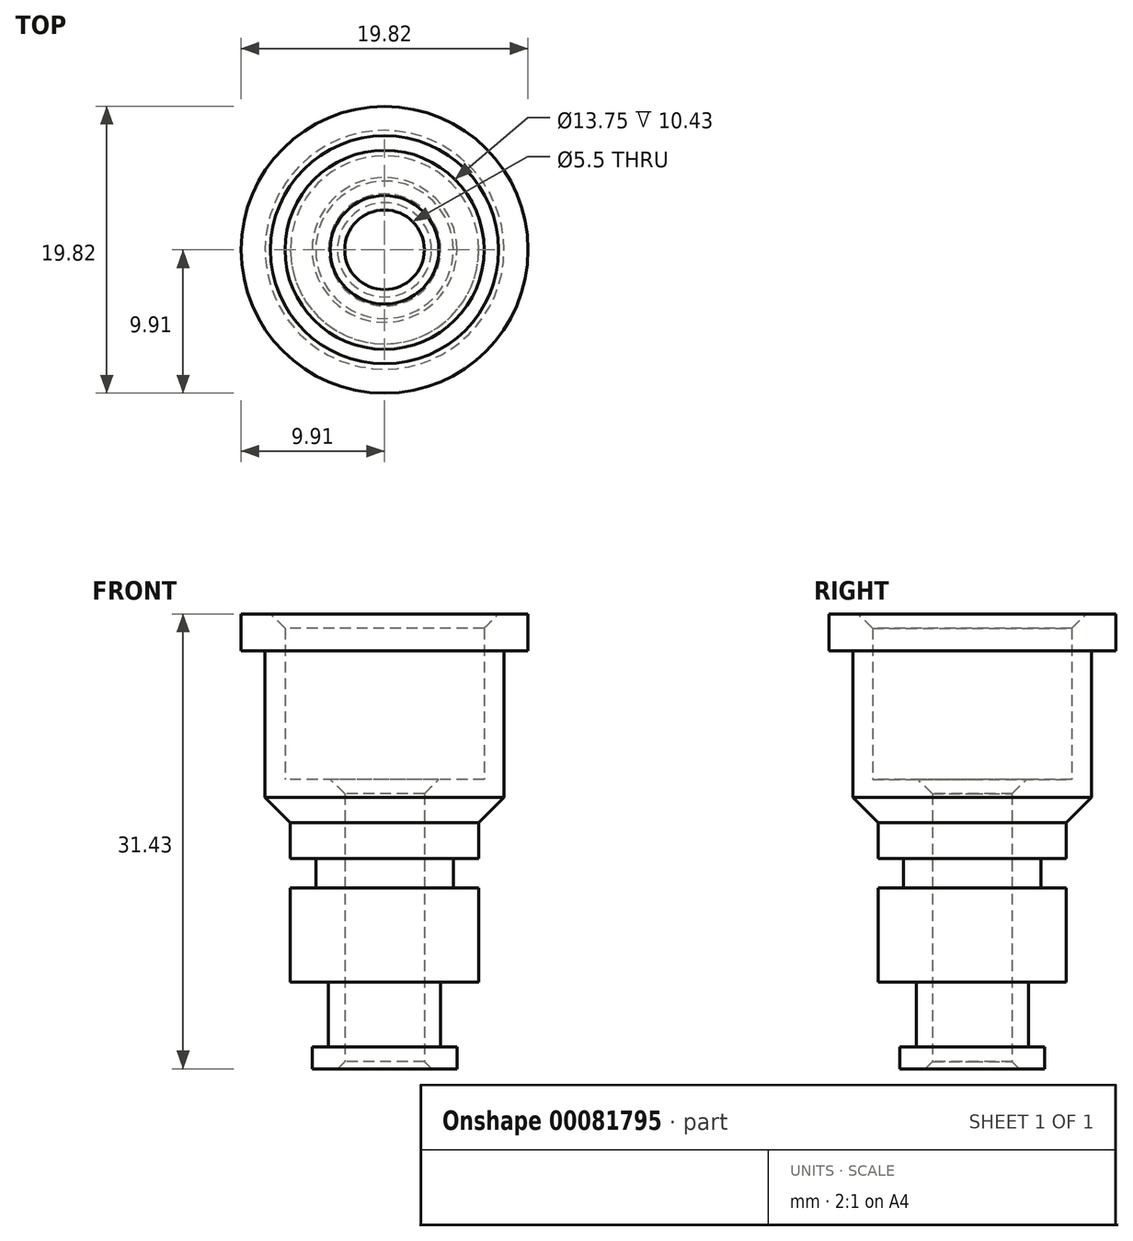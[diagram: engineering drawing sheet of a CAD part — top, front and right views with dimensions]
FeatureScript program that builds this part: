
annotation { "Feature Type Name" : "Feature", "Feature Type Description" : "" }
export const myFeature = defineFeature(function(context is Context, id is Id, definition is map)
    precondition{}
    {
        {
            var Q0;
            Q0=qCreatedBy(makeId("Top.planeOp"),FACE);
            var sketch = newSketch(context, id + "F0", { "sketchPlane" : qUnion([Q0])});
            skCircle(sketch, "E0", {"center": v(0, 0) * mm, "radius": 6.5 * mm});
            skCircle(sketch, "E1", {"center": v(0, 0) * mm, "radius": 2.75 * mm});
            skSolve(sketch);
        }
        {
            var Q0;
            Q0 = qSketchRegion(id + "F0", true);
            extrude(context, id + "F1", {"entities" : qUnion([Q0]), "depth" : 20 * mm});
        }
        {
            var Q0;
            Q0=makeQuery(id+"F1.opExtrude","CAP_FACE",FACE,{"disambiguationData":[OSD([sQuery(id+"F0.wireOp",EDGE,"E0"),sQuery(id+"F0.wireOp",EDGE,"E1")])],"isStart":true});
            var sketch = newSketch(context, id + "F2", { "sketchPlane" : qUnion([Q0])});
            skCircle(sketch, "E2.0", {"center": v(0, 0) * mm, "radius": 6.5 * mm});
            skCircle(sketch, "E3", {"center": v(0, 0) * mm, "radius": 5 * mm});
            skSolve(sketch);
        }
        {
            var Q0;
            Q0 = qSketchRegion(id + "F2", true);
            extrude(context, id + "F3", {"entities" : qUnion([Q0]), "operationType" : NewBodyOperationType.REMOVE, "oppositeDirection" : true, "depth" : 6 * mm});
        }
        {
            var Q0;
            Q0=makeQuery(id+"F3.boolean.opBoolean","COPY",FACE,{"derivedFrom":makeQuery(id+"F3.opExtrude","CAP_FACE",FACE,{"disambiguationData":[OSD([sQuery(id+"F2.wireOp",EDGE,"E2.0"),sQuery(id+"F2.wireOp",EDGE,"E3")])],"isStart":false})});
            var sketch = newSketch(context, id + "F4", { "sketchPlane" : qUnion([Q0])});
            skCircle(sketch, "E4.0", {"center": v(0, 0) * mm, "radius": 5 * mm});
            skCircle(sketch, "E5", {"center": v(0, 0) * mm, "radius": 3.88 * mm});
            skSolve(sketch);
        }
        {
            var Q0;
            Q0 = qSketchRegion(id + "F4", true);
            extrude(context, id + "F5", {"entities" : qUnion([Q0]), "operationType" : NewBodyOperationType.REMOVE, "depth" : 4.5 * mm});
        }
        {
            var Q0;
            Q0=makeQuery(id+"F1.opExtrude","CAP_FACE",FACE,{"disambiguationData":[OSD([sQuery(id+"F0.wireOp",EDGE,"E0"),sQuery(id+"F0.wireOp",EDGE,"E1")])],"isStart":true});
            cPlane(context, id + "F6", {"entities" : qUnion([Q0]), "cplaneType" : CPlaneType.OFFSET, "offset" : 12.5 * mm, "oppositeDirection" : true, "width" : 150 * mm, "height" : 150 * mm});
        }
        {
            var Q0;
            Q0=qCreatedBy(id+"F6.planeOp",FACE);
            var sketch = newSketch(context, id + "F7", { "sketchPlane" : qUnion([Q0])});
            skCircle(sketch, "E6.0", {"center": v(0, 0) * mm, "radius": 6.5 * mm});
            skCircle(sketch, "E7", {"center": v(0, 0) * mm, "radius": 4.75 * mm});
            skSolve(sketch);
        }
        {
            var Q0;
            Q0 = qSketchRegion(id + "F7", true);
            extrude(context, id + "F8", {"entities" : qUnion([Q0]), "operationType" : NewBodyOperationType.REMOVE, "oppositeDirection" : true, "depth" : 2.03 * mm});
        }
        {
            var Q0;
            Q0=makeQuery(id+"F1.opExtrude","CAP_FACE",FACE,{"disambiguationData":[OSD([sQuery(id+"F0.wireOp",EDGE,"E0"),sQuery(id+"F0.wireOp",EDGE,"E1")])],"isStart":false});
            var sketch = newSketch(context, id + "F9", { "sketchPlane" : qUnion([Q0])});
            skCircle(sketch, "E8.0", {"center": v(0, 0) * mm, "radius": 6.5 * mm});
            skCircle(sketch, "E9", {"center": v(0, 0) * mm, "radius": 8.25 * mm});
            skSolve(sketch);
        }
        {
            var Q0;
            Q0 = qSketchRegion(id + "F9", true);
            extrude(context, id + "F10", {"entities" : qUnion([Q0]), "operationType" : NewBodyOperationType.ADD, "oppositeDirection" : true, "depth" : 3 * mm});
        }
        {
            var Q0;
            Q0=makeQuery(id+"F10.boolean.opBoolean","MERGE",FACE,{"derivedFrom":[makeQuery(id+"F1.opExtrude","CAP_FACE",FACE,{"disambiguationData":[OSD([sQuery(id+"F0.wireOp",EDGE,"E0"),sQuery(id+"F0.wireOp",EDGE,"E1")])],"isStart":false}),makeQuery(id+"F10.opExtrude","CAP_FACE",FACE,{"disambiguationData":[OSD([sQuery(id+"F9.wireOp",EDGE,"E8.0"),sQuery(id+"F9.wireOp",EDGE,"E9")])],"isStart":true})]});
            var sketch = newSketch(context, id + "F11", { "sketchPlane" : qUnion([Q0])});
            skCircle(sketch, "E10", {"center": v(0, 0) * mm, "radius": 6.88 * mm});
            skCircle(sketch, "E11.0", {"center": v(0, 0) * mm, "radius": 8.25 * mm});
            skSolve(sketch);
        }
        {
            var Q0;
            Q0 = qSketchRegion(id + "F11", true);
            extrude(context, id + "F12", {"entities" : qUnion([Q0]), "operationType" : NewBodyOperationType.ADD, "depth" : 11.43 * mm});
        }
        {
            var Q0;
            Q0=makeQuery(id+"F12.opExtrude","CAP_FACE",FACE,{"disambiguationData":[OSD([sQuery(id+"F11.wireOp",EDGE,"E10"),sQuery(id+"F11.wireOp",EDGE,"E11.0")])],"isStart":false});
            var sketch = newSketch(context, id + "F13", { "sketchPlane" : qUnion([Q0])});
            skCircle(sketch, "E12.0", {"center": v(0, 0) * mm, "radius": 8.25 * mm});
            skCircle(sketch, "E13", {"center": v(0, 0) * mm, "radius": 9.9 * mm});
            skSolve(sketch);
        }
        {
            var Q0;
            Q0 = qSketchRegion(id + "F13", true);
            extrude(context, id + "F14", {"entities" : qUnion([Q0]), "operationType" : NewBodyOperationType.ADD, "oppositeDirection" : true, "depth" : 2.54 * mm});
        }
        {
            var Q0;
            Q0=makeQuery(id+"F10.opExtrude","CAP_EDGE",EDGE,{"disambiguationData":[OSD([sQuery(id+"F9.wireOp",EDGE,"E9")])],"isStart":false});
            chamfer(context, id + "F15", {"entities" : qUnion([Q0]), "width" : 1.75 * mm, "tangentPropagation" : true});
        }
        {
            var Q0;
            Q0=makeQuery(id+"F12.opExtrude","CAP_EDGE",EDGE,{"disambiguationData":[OSD([sQuery(id+"F11.wireOp",EDGE,"E10")])],"isStart":false});
            chamfer(context, id + "F16", {"entities" : qUnion([Q0]), "width" : 1 * mm, "tangentPropagation" : true});
        }
        {
            var Q0;
            Q0=makeQuery(id+"F1.opExtrude","CAP_EDGE",EDGE,{"disambiguationData":[OSD([sQuery(id+"F0.wireOp",EDGE,"E1")])],"isStart":true});
            chamfer(context, id + "F17", {"entities" : qUnion([Q0]), "width" : .5 * mm, "tangentPropagation" : true});
        }
        {
            var Q0;
            Q0=makeQuery(id+"F1.opExtrude","CAP_EDGE",EDGE,{"disambiguationData":[OSD([sQuery(id+"F0.wireOp",EDGE,"E1")])],"isStart":false});
            chamfer(context, id + "F18", {"entities" : qUnion([Q0]), "width" : 1 * mm, "tangentPropagation" : true});
        }
    });
